# Revit family: LENSES-ES1547xxWS8X0B0500
name_source: partatom
category: Oprawy oświetleniowe
revit_build: Autodesk Revit 2017 (Build: 20190508_0315(x64)
units: mm (PartAtom-declared; Revit-internal decimal feet)

## family parameters
Numer OmniClass = 23.80.70.11
Obiekt nadrzędny = Powierzchnia
Punkt obliczania pomieszczeń = Nie
Tnij formami wycięć po wczytaniu = Nie
Typ części = Normalny
Tytuł OmniClass = Luminaries for Internal Lighting
Współdzielony = Nie
Wymiar okrągłego złącza = Użyj średnicy
Źródło światła = Tak

## types (4) — shared parameters
Emituj kształt widoczny w renderingu = Nie
Emituj z długości prostokąta = 113 mm  [stored 0.370735 ft]
Emituj z szerokości prostokąta = 1471 mm  [stored 4.82612 ft]
Filtr koloru = 16777215
Kod zespołu = D5020200
Lampa = LED
Obciążenie pozorne = 31 VA
Odchylenie kierunku = 90.00°
Plik sieci fotometrycznej = LENSES-EQ0622NDWS840B0350.IES
Producent = RIDI Leuchten GmbH
URL = www.ridi.de
Zmiana temperatury barwowej przyciemniania lampy = <Brak>
brand = RIDI
conformity mark = CE
electrical safety class = 1
height = 60 mm  [stored 0.19685 ft]
ingress protection (IP) code = IP20
length = 1547 mm  [stored 5.07546 ft]
nominal frequency = 50-60Hz
nominal voltage = 230
rated input power = 31
voltage type (AC, DC, UC) = AC
weight = 6,1kg
width = 183 mm
zero-valued in all types: Domyślna rzędna

## per-type parameters (varying)
| type | Model |
| LENSES-ES1547NDWS830B0500 | 0827716 |
| LENSES-ES1547DAWS830B0500 | 0837725 |
| LENSES-ES1547NDWS840B0500 | 0827717 |
| LENSES-ES1547DAWS840B0500 | 0837717 |

note: column(s) folded — value = type name in every type: product name

note: [stored X ft] marks values corroborated as IEEE doubles in the binary element streams (Revit-internal decimal feet)
